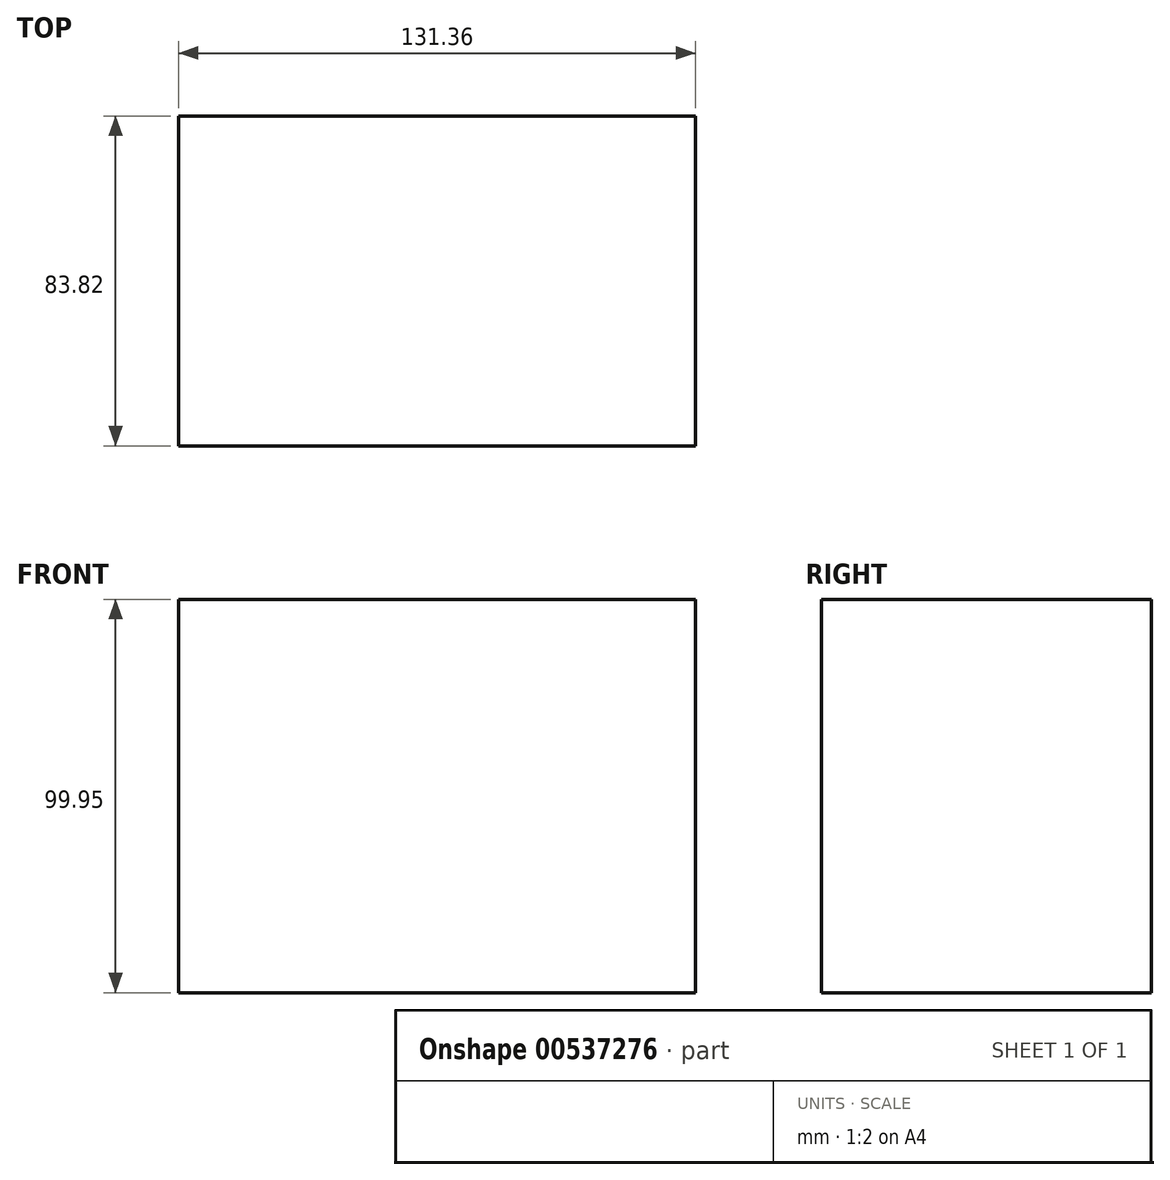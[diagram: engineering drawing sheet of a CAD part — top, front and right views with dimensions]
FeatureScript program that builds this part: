
annotation { "Feature Type Name" : "Feature", "Feature Type Description" : "" }
export const myFeature = defineFeature(function(context is Context, id is Id, definition is map)
    precondition{}
    {
        {
            var Q0;
            Q0=qCreatedBy(makeId("Front.planeOp"),FACE);
            var sketch = newSketch(context, id + "F0", { "sketchPlane" : qUnion([Q0])});
            skLineSegment(sketch, "E0.bottom", {"start": v(-62.25, 36.84) * mm, "end": v(69.1, 36.84) * mm});
            skLineSegment(sketch, "E0.top", {"start": v(-62.25, -63.11) * mm, "end": v(69.1, -63.11) * mm});
            skLineSegment(sketch, "E0.left", {"start": v(-62.25, 36.84) * mm, "end": v(-62.25, -63.11) * mm});
            skLineSegment(sketch, "E0.right", {"start": v(69.1, 36.84) * mm, "end": v(69.1, -63.11) * mm});
            skSolve(sketch);
        }
        {
            var Q0;
            Q0=makeQuery(id+"F0.imprint","IMPRINT",FACE,{"disambiguationData":[TD([[makeQuery(id+"F0.imprint","IMPRINT",EDGE,{"derivedFrom":sQuery(id+"F0.wireOp",EDGE,"E0.bottom")}),-1.0]])]});
            extrude(context, id + "F1", {"entities" : qUnion([Q0]), "depth" : 83.82 * mm, "offsetDistance" : 25.4 * mm});
        }
    });
